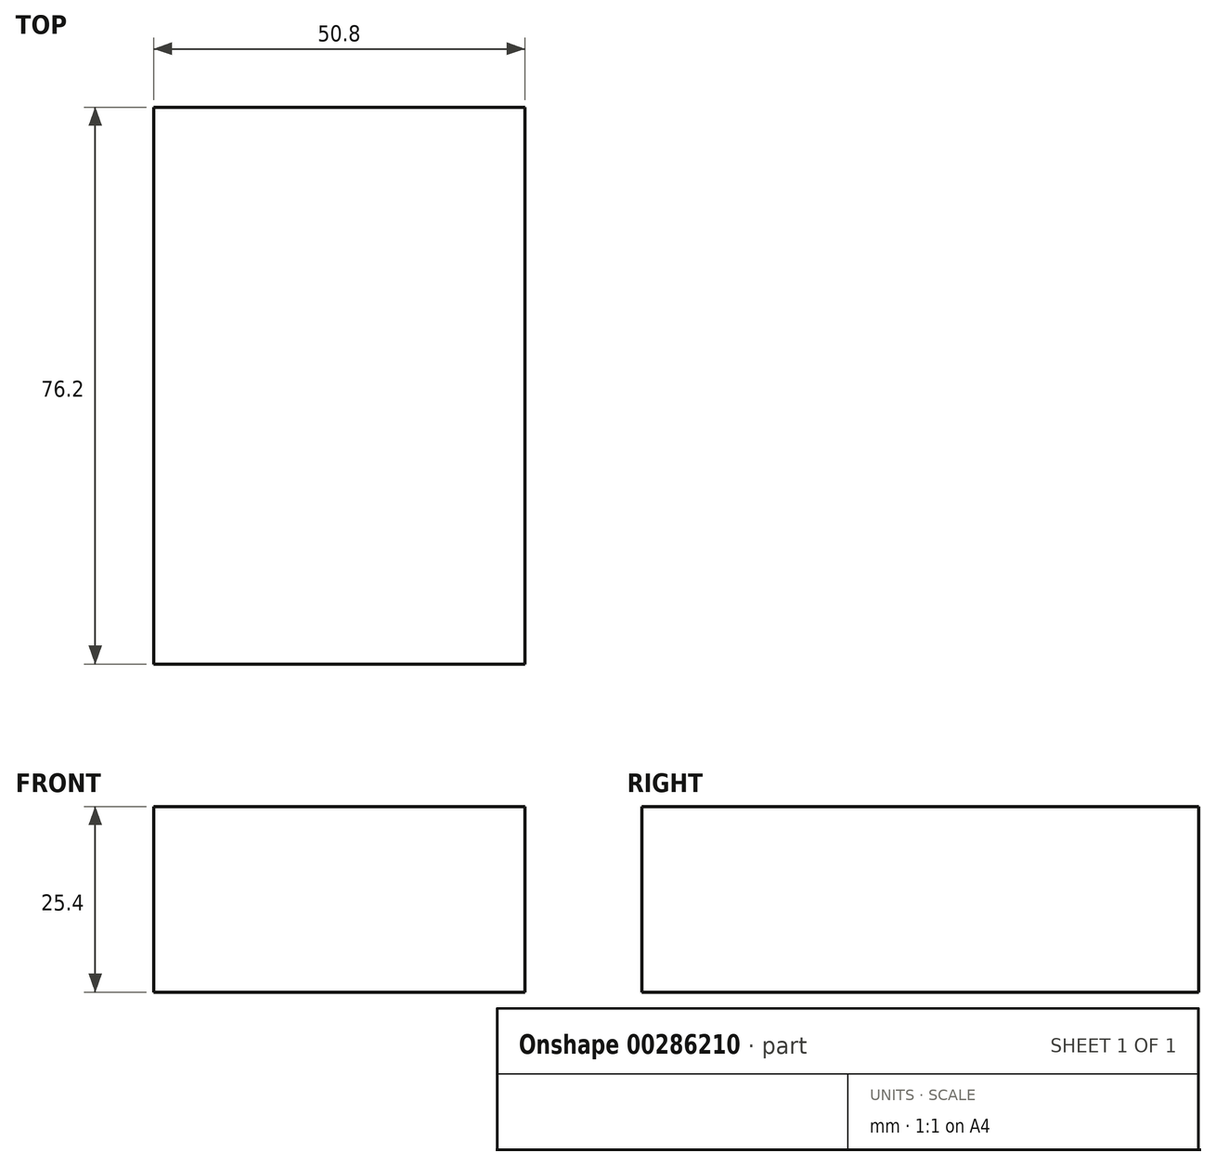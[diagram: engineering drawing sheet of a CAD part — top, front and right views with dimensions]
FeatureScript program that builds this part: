
annotation { "Feature Type Name" : "Feature", "Feature Type Description" : "" }
export const myFeature = defineFeature(function(context is Context, id is Id, definition is map)
    precondition{}
    {
        {
            var Q0;
            Q0=qCreatedBy(makeId("Top.planeOp"),FACE);
            var sketch = newSketch(context, id + "F0", { "sketchPlane" : qUnion([Q0])});
            skLineSegment(sketch, "E0.bottom", {"start": v(25.4, -38.1) * mm, "end": v(-25.4, -38.1) * mm});
            skLineSegment(sketch, "E0.top", {"start": v(25.4, 38.1) * mm, "end": v(-25.4, 38.1) * mm});
            skLineSegment(sketch, "E0.left", {"start": v(25.4, -38.1) * mm, "end": v(25.4, 38.1) * mm});
            skLineSegment(sketch, "E0.right", {"start": v(-25.4, -38.1) * mm, "end": v(-25.4, 38.1) * mm});
            skPoint(sketch, "E0.middle", {"position": v(0, 0) * mm});
            skSolve(sketch);
        }
        {
            var Q0;
            Q0 = qSketchRegion(id + "F0", true);
            extrude(context, id + "F1", {"entities" : qUnion([Q0]), "depth" : 25.4 * mm});
        }
    });
